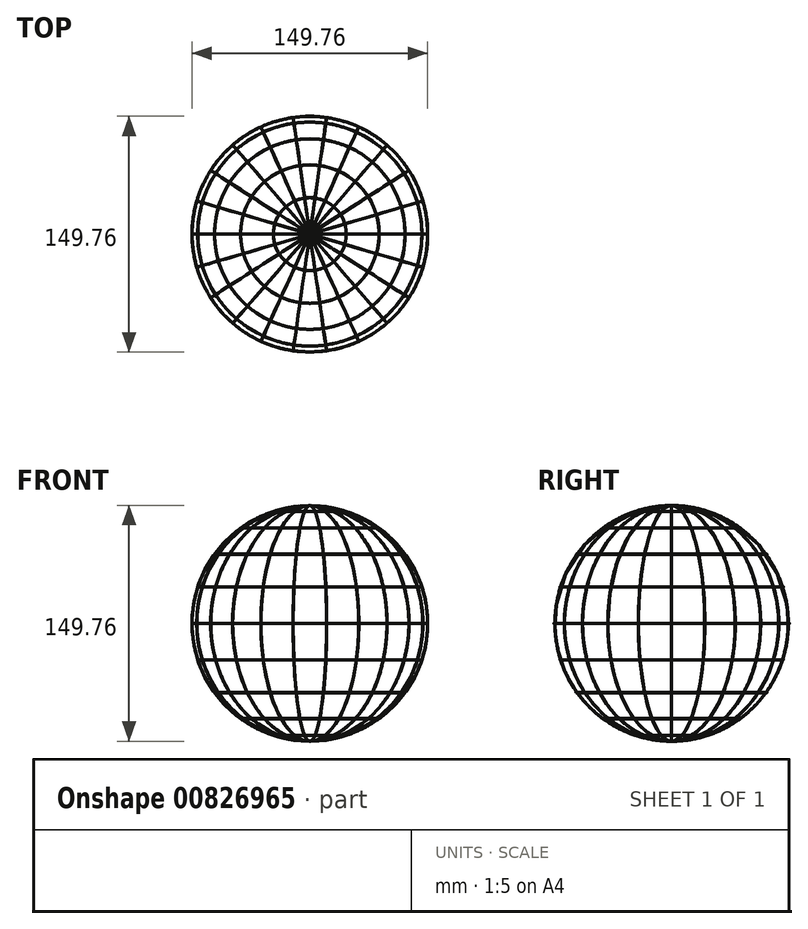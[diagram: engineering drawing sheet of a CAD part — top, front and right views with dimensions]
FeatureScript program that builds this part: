
annotation { "Feature Type Name" : "Feature", "Feature Type Description" : "" }
export const myFeature = defineFeature(function(context is Context, id is Id, definition is map)
    precondition{}
    {
        {
            var Q0;
            Q0=qCreatedBy(makeId("Front.planeOp"),FACE);
            var sketch = newSketch(context, id + "F0", { "sketchPlane" : qUnion([Q0])});
            skLineSegment(sketch, "E0", {"start": v(0, 0) * mm, "end": v(0, 74.83) * mm});
            skPoint(sketch, "E1.center", {"position": v(0, 0) * mm});
            skPoint(sketch, "E2", {"position": v(0, 74.83) * mm});
            skCircle(sketch, "E3", {"center": v(0, 74.83) * mm, "radius": 0.05 * mm});
            skCircle(sketch, "E4.1.0", {"center": v(23.12, 71.17) * mm, "radius": 0.05 * mm});
            skCircle(sketch, "E4.2.0", {"center": v(43.98, 60.54) * mm, "radius": 0.05 * mm});
            skLineSegment(sketch, "E4.anchor1", {"start": v(0, 0) * mm, "end": v(0, 74.83) * mm, "construction": true});
            skLineSegment(sketch, "E4.anchor2", {"start": v(0, 0) * mm, "end": v(0, -74.83) * mm, "construction": true});
            skCircle(sketch, "E5.1.3.0", {"center": v(60.54, 43.98) * mm, "radius": 0.05 * mm});
            skCircle(sketch, "E5.1.4.0", {"center": v(71.17, 23.12) * mm, "radius": 0.05 * mm});
            skCircle(sketch, "E5.1.5.0", {"center": v(74.83, 0) * mm, "radius": 0.05 * mm});
            skCircle(sketch, "E5.1.6.0", {"center": v(71.17, -23.12) * mm, "radius": 0.05 * mm});
            skCircle(sketch, "E5.1.7.0", {"center": v(60.54, -43.98) * mm, "radius": 0.05 * mm});
            skCircle(sketch, "E5.1.8.0", {"center": v(43.98, -60.54) * mm, "radius": 0.05 * mm});
            skCircle(sketch, "E5.1.9.0", {"center": v(23.12, -71.17) * mm, "radius": 0.05 * mm});
            skCircle(sketch, "E6.1.10.0", {"center": v(0, -74.83) * mm, "radius": 0.05 * mm});
            skArc(sketch, "E7", {"start": v(0, 74.83) * mm, "mid": v(-74.83, -0.02) * mm, "end": v(0.05, -74.83) * mm});
            skSolve(sketch);
        }
        {
            var Q0;
            Q0=makeQuery(id+"F0.imprint","IMPRINT",FACE,{"disambiguationData":[TD([[makeQuery(id+"F0.imprint","IMPRINT",EDGE,{"derivedFrom":sQuery(id+"F0.wireOp",EDGE,"E5.1.3.0")}),1.0]])]});
            var Q1;
            Q1=makeQuery(id+"F0.imprint","IMPRINT",FACE,{"disambiguationData":[TD([[makeQuery(id+"F0.imprint","IMPRINT",EDGE,{"derivedFrom":sQuery(id+"F0.wireOp",EDGE,"E4.1.0")}),1.0]])]});
            var Q2;
            Q2=makeQuery(id+"F0.imprint","IMPRINT",FACE,{"disambiguationData":[TD([[makeQuery(id+"F0.imprint","IMPRINT",EDGE,{"derivedFrom":sQuery(id+"F0.wireOp",EDGE,"E5.1.7.0")}),1.0]])]});
            var Q3;
            Q3=makeQuery(id+"F0.imprint","IMPRINT",FACE,{"disambiguationData":[TD([[makeQuery(id+"F0.imprint","IMPRINT",EDGE,{"derivedFrom":sQuery(id+"F0.wireOp",EDGE,"E4.2.0")}),1.0]])]});
            var Q4;
            Q4=makeQuery(id+"F0.imprint","IMPRINT",FACE,{"disambiguationData":[TD([[makeQuery(id+"F0.imprint","IMPRINT",EDGE,{"derivedFrom":sQuery(id+"F0.wireOp",EDGE,"E5.1.9.0")}),1.0]])]});
            var Q5;
            Q5=makeQuery(id+"F0.imprint","IMPRINT",FACE,{"disambiguationData":[TD([[makeQuery(id+"F0.imprint","IMPRINT",EDGE,{"derivedFrom":sQuery(id+"F0.wireOp",EDGE,"E5.1.4.0")}),1.0]])]});
            var Q6;
            Q6=makeQuery(id+"F0.imprint","IMPRINT",FACE,{"disambiguationData":[TD([[makeQuery(id+"F0.imprint","IMPRINT",EDGE,{"derivedFrom":sQuery(id+"F0.wireOp",EDGE,"E5.1.6.0")}),1.0]])]});
            var Q7;
            Q7=makeQuery(id+"F0.imprint","IMPRINT",FACE,{"disambiguationData":[TD([[makeQuery(id+"F0.imprint","IMPRINT",EDGE,{"derivedFrom":sQuery(id+"F0.wireOp",EDGE,"E5.1.8.0")}),1.0]])]});
            var Q8;
            Q8=makeQuery(id+"F0.imprint","IMPRINT",FACE,{"disambiguationData":[TD([[makeQuery(id+"F0.imprint","IMPRINT",EDGE,{"derivedFrom":sQuery(id+"F0.wireOp",EDGE,"E5.1.5.0")}),1.0]])]});
            var Q9;
            Q9=sQuery(id+"F0.wireOp",EDGE,"E4.2.0");
            var Q10;
            Q10=sQuery(id+"F0.wireOp",EDGE,"E5.1.4.0");
            var Q11;
            Q11=sQuery(id+"F0.wireOp",EDGE,"E5.1.6.0");
            var Q12;
            Q12=sQuery(id+"F0.wireOp",EDGE,"E4.1.0");
            var Q13;
            Q13=sQuery(id+"F0.wireOp",EDGE,"E5.1.8.0");
            var Q14;
            Q14=sQuery(id+"F0.wireOp",EDGE,"E5.1.9.0");
            var Q15;
            Q15=sQuery(id+"F0.wireOp",EDGE,"E5.1.3.0");
            var Q16;
            Q16=sQuery(id+"F0.wireOp",EDGE,"E5.1.5.0");
            var Q17;
            Q17=sQuery(id+"F0.wireOp",EDGE,"E5.1.7.0");
            var Q18;
            Q18=sQuery(id+"F0.wireOp",EDGE,"E6.1.10.0");
            var Q19;
            Q19=sQuery(id+"F0.wireOp",EDGE,"E3");
            var Q20;
            Q20=sQuery(id+"F0.wireOp",EDGE,"E0");
            revolve(context, id + "F1", {"surfaceOperationType" : NewSurfaceOperationType.NEW, "entities" : qUnion([Q0, Q1, Q2, Q3, Q4, Q5, Q6, Q7, Q8]), "surfaceEntities" : qUnion([Q9, Q10, Q11, Q12, Q13, Q14, Q15, Q16, Q17, Q18, Q19]), "axis" : qUnion([Q20]), "revolveType" : RevolveType.FULL});
        }
        {
            var Q0;
            Q0=qCreatedBy(makeId("Right.planeOp"),FACE);
            var sketch = newSketch(context, id + "F2", { "sketchPlane" : qUnion([Q0])});
            skCircle(sketch, "E8", {"center": v(0, 74.83) * mm, "radius": 0.05 * mm});
            skSolve(sketch);
        }
        {
            var Q0;
            Q0=makeQuery(id+"F2.imprint","IMPRINT",FACE,{"disambiguationData":[TD([[makeQuery(id+"F2.imprint","IMPRINT",EDGE,{"derivedFrom":sQuery(id+"F2.wireOp",EDGE,"E8")}),1.0]])]});
            var Q1;
            Q1=sQuery(id+"F2.wireOp",EDGE,"E8");
            var Q2;
            Q2=sQuery(id+"F0.wireOp",EDGE,"E7");
            sweep(context, id + "F3", {"profiles" : qUnion([Q0]), "surfaceProfiles" : qUnion([Q1]), "path" : qUnion([Q2])});
        }
        {
            var Q0;
            Q0=makeQuery(id+"F3.opSweep","SWEPT_BODY",BODY,{"disambiguationData":[OSD([sQuery(id+"F0.wireOp",EDGE,"E7"),sQuery(id+"F2.wireOp",EDGE,"E8")])]});
            var Q1;
            Q1=sQuery(id+"F0.wireOp",EDGE,"E0");
            circularPattern(context, id + "F4", {"entities" : qUnion([Q0]), "axis" : qUnion([Q1]), "angle" : 360 * degree, "instanceCount" : 22, "equalSpace" : true});
        }
    });
